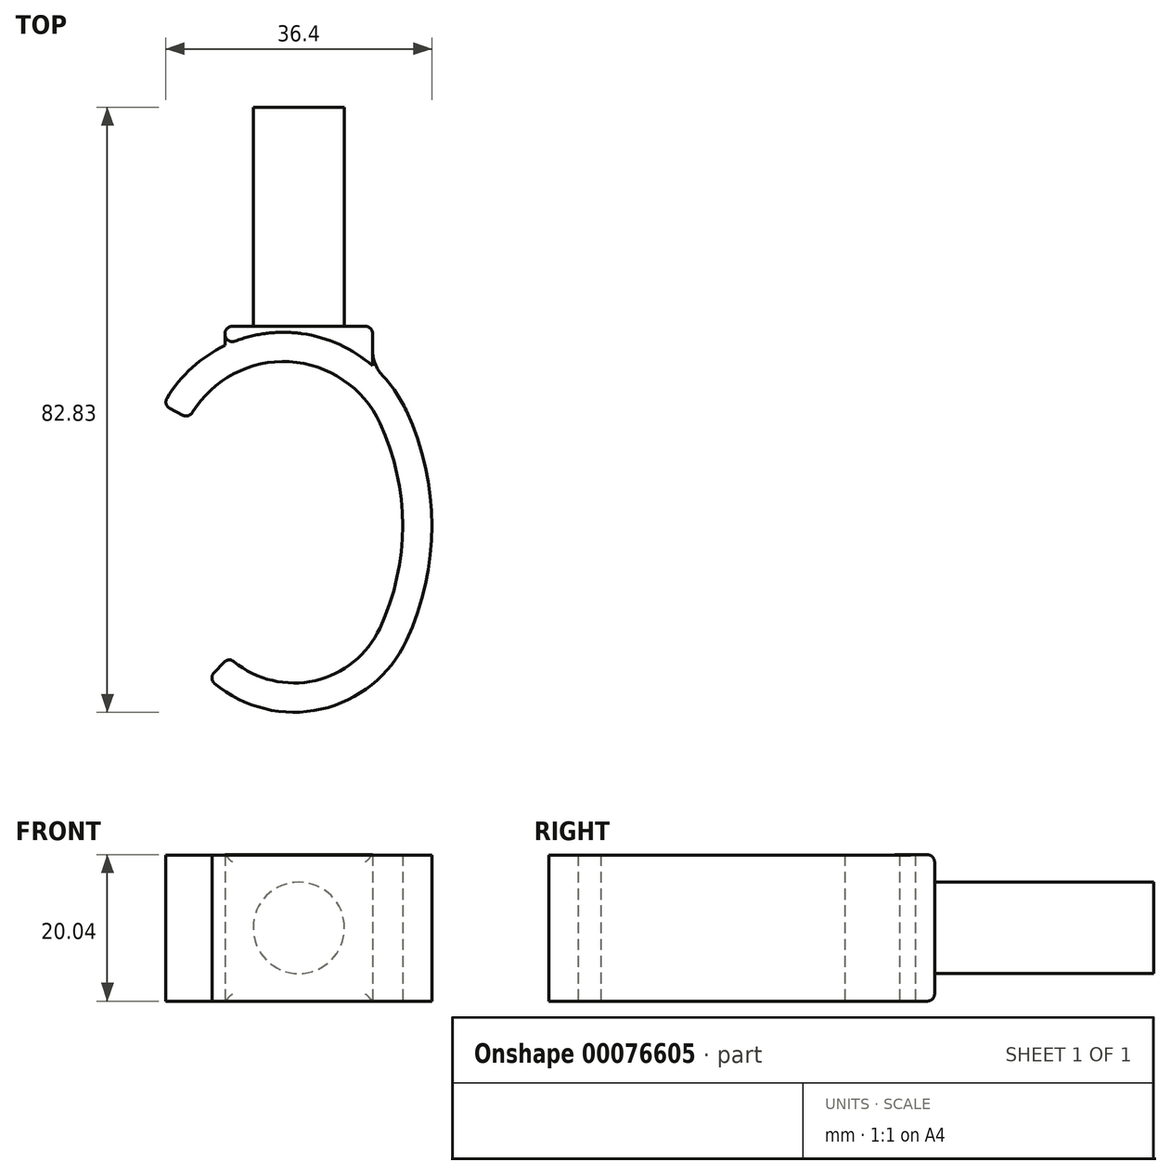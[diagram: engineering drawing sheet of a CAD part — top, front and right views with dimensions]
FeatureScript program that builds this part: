
annotation { "Feature Type Name" : "Feature", "Feature Type Description" : "" }
export const myFeature = defineFeature(function(context is Context, id is Id, definition is map)
    precondition{}
    {
        {
            var Q0;
            Q0=qCreatedBy(makeId("Top.planeOp"),FACE);
            var sketch = newSketch(context, id + "F0", { "sketchPlane" : qUnion([Q0])});
            skArc(sketch, "E0", {"start": v(9.83, 11.74) * mm, "mid": v(-3.04, 20.17) * mm, "end": v(-16.3, 12.38) * mm});
            skArc(sketch, "E1", {"start": v(9.83, -16.33) * mm, "mid": v(12.94, -2.3) * mm, "end": v(9.83, 11.74) * mm});
            skArc(sketch, "E2", {"start": v(-10.85, -20.28) * mm, "mid": v(0.5, -23.6) * mm, "end": v(9.83, -16.33) * mm});
            skLineSegment(sketch, "E3", {"start": v(-25.06, 20.17) * mm, "end": v(26.9, 20.17) * mm, "construction": true});
            skLineSegment(sketch, "E4", {"start": v(-21.47, -23.83) * mm, "end": v(16.97, -23.83) * mm, "construction": true});
            skArc(sketch, "E5.0", {"start": v(13.46, 13.43) * mm, "mid": v(-2.94, 24.17) * mm, "end": v(-19.84, 14.24) * mm});
            skArc(sketch, "E5.1", {"start": v(13.46, -18.01) * mm, "mid": v(16.94, -2.3) * mm, "end": v(13.46, 13.43) * mm});
            skArc(sketch, "E5.2", {"start": v(-13.6, -23.19) * mm, "mid": v(1.25, -27.52) * mm, "end": v(13.46, -18.01) * mm});
            skLineSegment(sketch, "E6", {"start": v(-19.84, 14.24) * mm, "end": v(-16.3, 12.38) * mm});
            skLineSegment(sketch, "E7", {"start": v(-13.6, -23.19) * mm, "end": v(-10.85, -20.28) * mm});
            skSolve(sketch);
        }
        {
            var Q0;
            Q0=makeQuery(id+"F0.imprint","IMPRINT",FACE,{"disambiguationData":[TD([[makeQuery(id+"F0.imprint","IMPRINT",EDGE,{"derivedFrom":sQuery(id+"F0.wireOp",EDGE,"E0")}),-1.0]])]});
            extrude(context, id + "F1", {"entities" : qUnion([Q0]), "depth" : 20 * mm});
        }
        {
            var Q0;
            Q0=qCreatedBy(makeId("Front.planeOp"),FACE);
            cPlane(context, id + "F2", {"entities" : qUnion([Q0]), "cplaneType" : CPlaneType.OFFSET, "offset" : 25 * mm, "oppositeDirection" : true, "width" : 150 * mm, "height" : 150 * mm});
        }
        {
            var Q0;
            Q0=qCreatedBy(id+"F2.planeOp",FACE);
            var sketch = newSketch(context, id + "F3", { "sketchPlane" : qUnion([Q0])});
            skLineSegment(sketch, "E8.bottom", {"start": v(8.84, 20.04) * mm, "end": v(-11.37, 20.04) * mm});
            skLineSegment(sketch, "E8.top", {"start": v(8.84, 0) * mm, "end": v(-11.37, 0) * mm});
            skLineSegment(sketch, "E8.left", {"start": v(8.84, 20.04) * mm, "end": v(8.84, 0) * mm});
            skLineSegment(sketch, "E8.right", {"start": v(-11.37, 20.04) * mm, "end": v(-11.37, 0) * mm});
            skSolve(sketch);
        }
        {
            var Q0;
            Q0 = qSketchRegion(id + "F3", true);
            var Q1;
            Q1=makeQuery(id+"F1.opExtrude","SWEPT_FACE",FACE,{"disambiguationData":[OSD([sQuery(id+"F0.wireOp",EDGE,"E5.0")])]});
            extrude(context, id + "F4", {"entities" : qUnion([Q0]), "operationType" : NewBodyOperationType.ADD, "endBound" : BoundingType.UP_TO_SURFACE, "endBoundEntityFace" : qUnion([Q1]), "depth" : 25 * mm});
        }
        {
            var Q0;
            Q0=makeQuery(id+"F1.opExtrude","SWEPT_EDGE",EDGE,{"disambiguationData":[OSD([sQuery(id+"F0.wireOp",EDGE,"E0"),sQuery(id+"F0.wireOp",EDGE,"E6")])]});
            var Q1;
            Q1=makeQuery(id+"F1.opExtrude","SWEPT_EDGE",EDGE,{"disambiguationData":[OSD([sQuery(id+"F0.wireOp",EDGE,"E5.0"),sQuery(id+"F0.wireOp",EDGE,"E6")])]});
            var Q2;
            Q2=makeQuery(id+"F1.opExtrude","SWEPT_EDGE",EDGE,{"disambiguationData":[OSD([sQuery(id+"F0.wireOp",EDGE,"E2"),sQuery(id+"F0.wireOp",EDGE,"E7")])]});
            var Q3;
            Q3=makeQuery(id+"F1.opExtrude","SWEPT_EDGE",EDGE,{"disambiguationData":[OSD([sQuery(id+"F0.wireOp",EDGE,"E5.2"),sQuery(id+"F0.wireOp",EDGE,"E7")])]});
            fillet(context, id + "F5", {"entities" : qUnion([Q0, Q1, Q2, Q3]), "radius" : 1 * mm, "tangentPropagation" : true, "allowEdgeOverflow" : false});
        }
        {
            var Q0;
            {var subQ0=sQuery(id+"F3.wireOp",EDGE,"E8.left");Q0=makeQuery(id+"F4.boolean.opBoolean","SPLIT",EDGE,{"disambiguationData":[topologyDisambiguationEdgeConnected([makeQuery(id+"F1.opExtrude","SWEPT_FACE",FACE,{"disambiguationData":[OSD([sQuery(id+"F0.wireOp",EDGE,"E5.0")])]})])],"derivedFrom":makeQuery(id+"F4.opExtrude","CAP_EDGE",EDGE,{"disambiguationData":[OSD([subQ0])],"isStart":false})});}
            fillet(context, id + "F6", {"entities" : qUnion([Q0]), "radius" : 5 * mm, "tangentPropagation" : true, "allowEdgeOverflow" : false});
        }
        {
            var Q0;
            {var subQ0=sQuery(id+"F3.wireOp",EDGE,"E8.right");Q0=makeQuery(id+"F4.boolean.opBoolean","SPLIT",EDGE,{"disambiguationData":[topologyDisambiguationEdgeConnected([makeQuery(id+"F1.opExtrude","SWEPT_FACE",FACE,{"disambiguationData":[OSD([sQuery(id+"F0.wireOp",EDGE,"E5.0")])]})])],"derivedFrom":makeQuery(id+"F4.opExtrude","CAP_EDGE",EDGE,{"disambiguationData":[OSD([subQ0])],"isStart":false})});}
            fillet(context, id + "F7", {"entities" : qUnion([Q0]), "radius" : 1 * mm, "tangentPropagation" : true, "allowEdgeOverflow" : false});
        }
        {
            var Q0;
            Q0=makeQuery(id+"F4.opExtrude","CAP_FACE",FACE,{"disambiguationData":[OSD([sQuery(id+"F3.wireOp",EDGE,"E8.bottom"),sQuery(id+"F3.wireOp",EDGE,"E8.top"),sQuery(id+"F3.wireOp",EDGE,"E8.left"),sQuery(id+"F3.wireOp",EDGE,"E8.right")])],"isStart":true});
            var sketch = newSketch(context, id + "F8", { "sketchPlane" : qUnion([Q0])});
            skLineSegment(sketch, "E9", {"start": v(-8.84, 10.02) * mm, "end": v(11.37, 10.02) * mm, "construction": true});
            skLineSegment(sketch, "E10", {"start": v(1.26, 20.04) * mm, "end": v(1.26, 0) * mm, "construction": true});
            skCircle(sketch, "E11", {"center": v(1.26, 10.02) * mm, "radius": 6.25 * mm});
            skSolve(sketch);
        }
        {
            var Q0;
            Q0 = qSketchRegion(id + "F8", true);
            extrude(context, id + "F9", {"entities" : qUnion([Q0]), "operationType" : NewBodyOperationType.ADD, "depth" : 30 * mm});
        }
        {
            var Q0;
            Q0=makeQuery(id+"F4.opExtrude","CAP_EDGE",EDGE,{"disambiguationData":[OSD([sQuery(id+"F3.wireOp",EDGE,"E8.bottom")])],"isStart":true});
            var Q1;
            Q1=makeQuery(id+"F4.opExtrude","CAP_EDGE",EDGE,{"disambiguationData":[OSD([sQuery(id+"F3.wireOp",EDGE,"E8.left")])],"isStart":true});
            var Q2;
            Q2=makeQuery(id+"F4.opExtrude","CAP_EDGE",EDGE,{"disambiguationData":[OSD([sQuery(id+"F3.wireOp",EDGE,"E8.right")])],"isStart":true});
            var Q3;
            Q3=makeQuery(id+"F4.opExtrude","CAP_EDGE",EDGE,{"disambiguationData":[OSD([sQuery(id+"F3.wireOp",EDGE,"E8.top")])],"isStart":true});
            fillet(context, id + "F10", {"entities" : qUnion([Q0, Q1, Q2, Q3]), "radius" : 1 * mm, "tangentPropagation" : true, "allowEdgeOverflow" : false});
        }
    });
